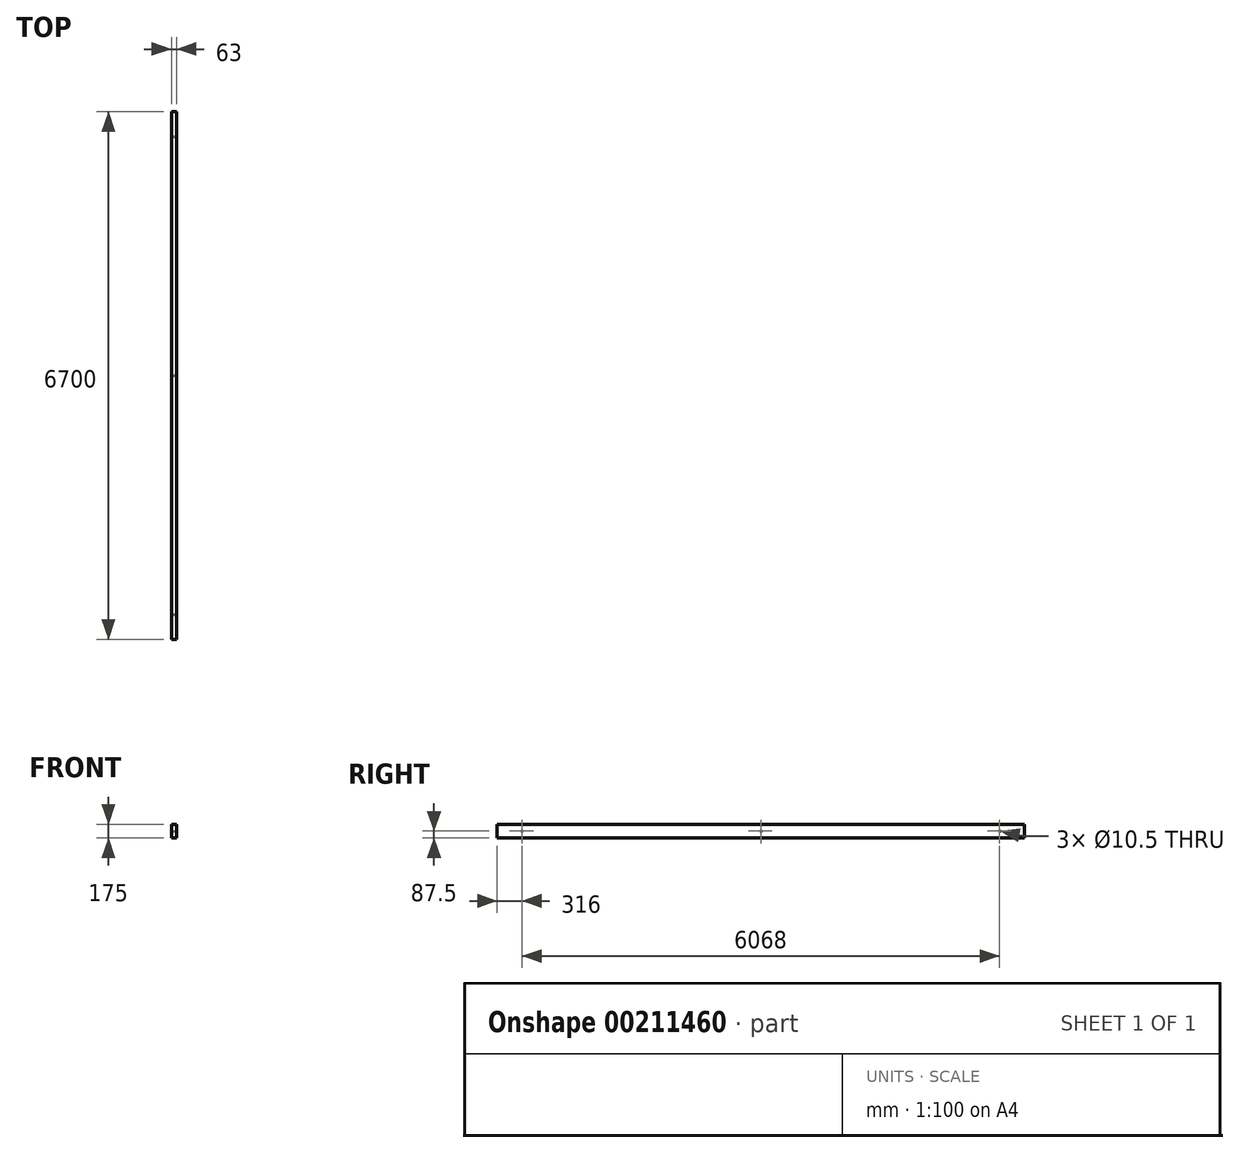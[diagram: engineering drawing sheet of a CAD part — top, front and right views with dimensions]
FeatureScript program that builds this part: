
annotation { "Feature Type Name" : "Feature", "Feature Type Description" : "" }
export const myFeature = defineFeature(function(context is Context, id is Id, definition is map)
    precondition{}
    {
        {
            var Q0;
            Q0=qCreatedBy(makeId("Front.planeOp"),FACE);
            var sketch = newSketch(context, id + "F0", { "sketchPlane" : qUnion([Q0])});
            skLineSegment(sketch, "E0.bottom", {"start": v(31.5, 87.5) * mm, "end": v(-31.5, 87.5) * mm});
            skLineSegment(sketch, "E0.top", {"start": v(31.5, -87.5) * mm, "end": v(-31.5, -87.5) * mm});
            skLineSegment(sketch, "E0.left", {"start": v(31.5, 87.5) * mm, "end": v(31.5, -87.5) * mm});
            skLineSegment(sketch, "E0.right", {"start": v(-31.5, 87.5) * mm, "end": v(-31.5, -87.5) * mm});
            skPoint(sketch, "E0.middle", {"position": v(0, 0) * mm});
            skSolve(sketch);
        }
        {
            var Q0;
            Q0=qSketchRegion(id+"F0",true);
            extrude(context, id + "F1", {"entities" : qUnion([Q0]), "depth" : 6700 * mm, "symmetric" : true});
        }
        {
            var Q0;
            Q0=makeQuery(id+"F1.opExtrude","SWEPT_FACE",FACE,{"disambiguationData":[OSD([sQuery(id+"F0.wireOp",EDGE,"E0.left")])]});
            var sketch = newSketch(context, id + "F2", { "sketchPlane" : qUnion([Q0])});
            skCircle(sketch, "E1", {"center": v(-3034, 0) * mm, "radius": 5.25 * mm});
            skCircle(sketch, "E2", {"center": v(3034, 0) * mm, "radius": 5.25 * mm});
            skCircle(sketch, "E3", {"center": v(0, 0) * mm, "radius": 5.25 * mm});
            skSolve(sketch);
        }
        {
            var Q0;
            Q0=qSketchRegion(id+"F2",true);
            extrude(context, id + "F3", {"entities" : qUnion([Q0]), "operationType" : NewBodyOperationType.REMOVE, "endBound" : BoundingType.THROUGH_ALL, "oppositeDirection" : true, "depth" : 25 * mm});
        }
    });
